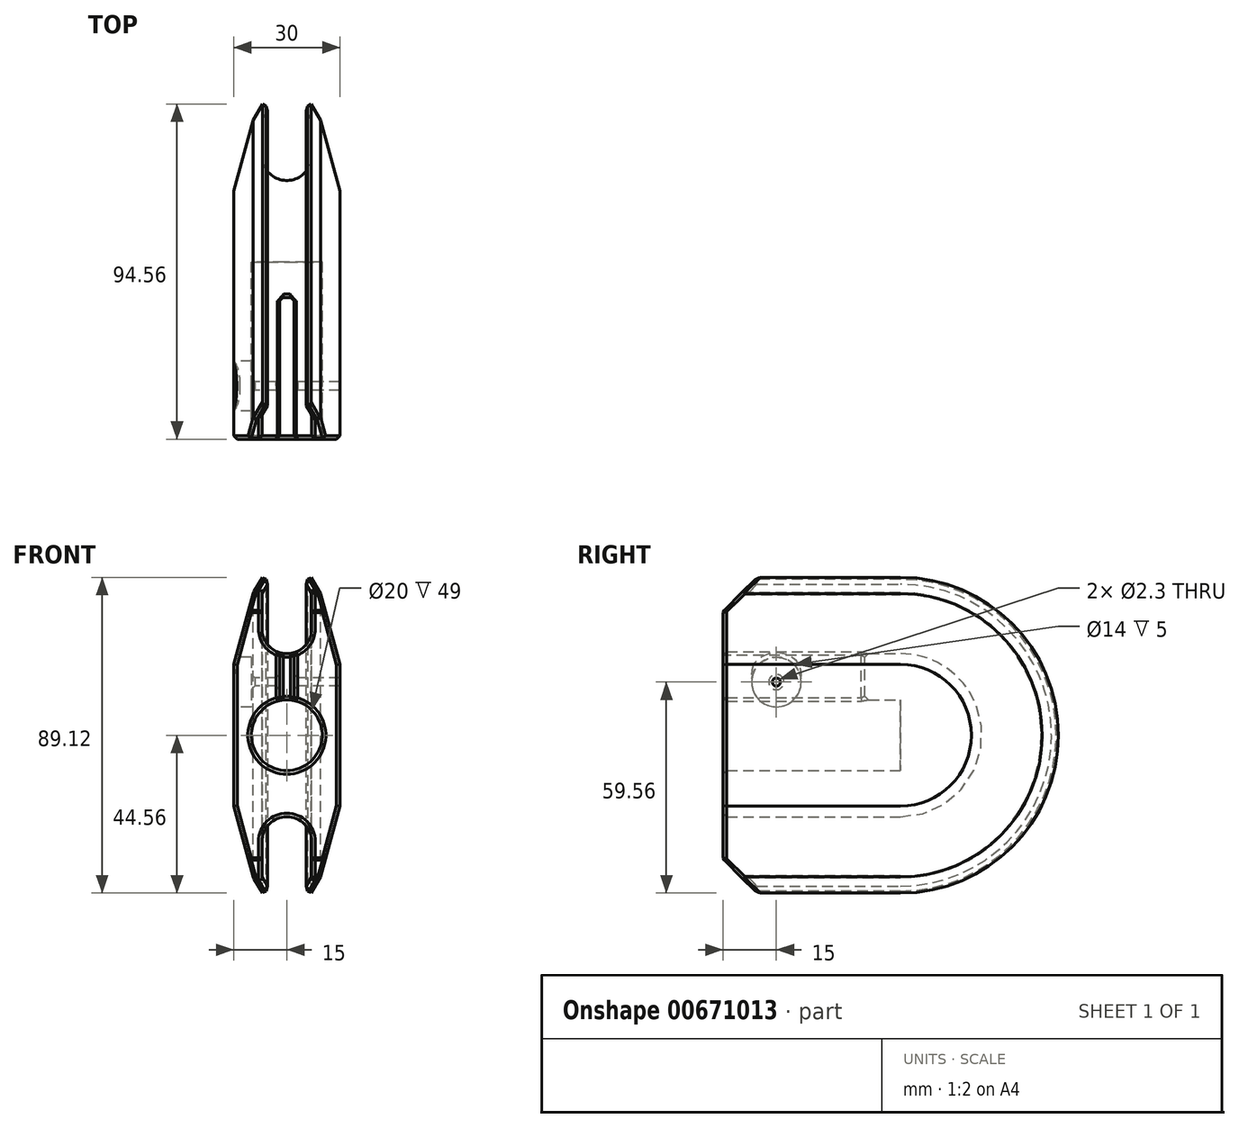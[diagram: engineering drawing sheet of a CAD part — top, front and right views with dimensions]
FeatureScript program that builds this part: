
annotation { "Feature Type Name" : "Feature", "Feature Type Description" : "" }
export const myFeature = defineFeature(function(context is Context, id is Id, definition is map)
    precondition{}
    {
        {
            var Q0;
            Q0=qCreatedBy(makeId("Front.planeOp"),FACE);
            var sketch = newSketch(context, id + "F0", { "sketchPlane" : qUnion([Q0])});
            skCircle(sketch, "E0", {"center": v(0, 0) * mm, "radius": 10 * mm});
            skLineSegment(sketch, "E1", {"start": v(-59.38, 0) * mm, "end": v(62.6, 0) * mm, "construction": true});
            skLineSegment(sketch, "E2", {"start": v(0, 56) * mm, "end": v(0, -52.42) * mm, "construction": true});
            skArc(sketch, "E3", {"start": v(-7, 30) * mm, "mid": v(0, 23) * mm, "end": v(7, 30) * mm});
            skLineSegment(sketch, "E4", {"start": v(7, 30) * mm, "end": v(7, 40) * mm});
            skLineSegment(sketch, "E5", {"start": v(7, 40) * mm, "end": v(5, 43.46) * mm});
            skLineSegment(sketch, "E6", {"start": v(5, 43.46) * mm, "end": v(6.9, 44.56) * mm});
            skLineSegment(sketch, "E7", {"start": v(6.9, 44.56) * mm, "end": v(9.54, 40) * mm});
            skLineSegment(sketch, "E8", {"start": v(9.54, 40) * mm, "end": v(15, 20) * mm});
            skLineSegment(sketch, "E9.MirrorCS", {"start": v(-9.54, 40) * mm, "end": v(-15, 20) * mm});
            skLineSegment(sketch, "E10.MirrorCS", {"start": v(-7, 30) * mm, "end": v(-7, 40) * mm});
            skLineSegment(sketch, "E11.MirrorCS", {"start": v(-5, 43.46) * mm, "end": v(-6.9, 44.56) * mm});
            skLineSegment(sketch, "E12.MirrorCS", {"start": v(-7, 40) * mm, "end": v(-5, 43.46) * mm});
            skLineSegment(sketch, "E13.MirrorCS", {"start": v(-6.9, 44.56) * mm, "end": v(-9.54, 40) * mm});
            skLineSegment(sketch, "E14.MirrorCS", {"start": v(-6.9, -44.56) * mm, "end": v(-9.54, -40) * mm});
            skLineSegment(sketch, "E15.MirrorCS", {"start": v(-7, -40) * mm, "end": v(-5, -43.46) * mm});
            skLineSegment(sketch, "E16.MirrorCS", {"start": v(-5, -43.46) * mm, "end": v(-6.9, -44.56) * mm});
            skLineSegment(sketch, "E17.MirrorCS", {"start": v(6.9, -44.56) * mm, "end": v(9.54, -40) * mm});
            skLineSegment(sketch, "E18.MirrorCS", {"start": v(7, -40) * mm, "end": v(5, -43.46) * mm});
            skLineSegment(sketch, "E19.MirrorCS", {"start": v(5, -43.46) * mm, "end": v(6.9, -44.56) * mm});
            skLineSegment(sketch, "E20.MirrorCS", {"start": v(-7, -30) * mm, "end": v(-7, -40) * mm});
            skLineSegment(sketch, "E21.MirrorCS", {"start": v(-9.54, -40) * mm, "end": v(-15, -20) * mm});
            skLineSegment(sketch, "E22.MirrorCS", {"start": v(9.54, -40) * mm, "end": v(15, -20) * mm});
            skLineSegment(sketch, "E23.MirrorCS", {"start": v(7, -30) * mm, "end": v(7, -40) * mm});
            skArc(sketch, "E24.MirrorCS", {"start": v(-7, -30) * mm, "mid": v(0, -23) * mm, "end": v(7, -30) * mm});
            skLineSegment(sketch, "E25", {"start": v(-15, 0) * mm, "end": v(15, 0) * mm});
            skLineSegment(sketch, "E26", {"start": v(-15, 20) * mm, "end": v(-15, -20) * mm});
            skLineSegment(sketch, "E27", {"start": v(15, 20) * mm, "end": v(15, -20) * mm});
            skSolve(sketch);
        }
        {
            var Q0;
            Q0 = qSketchRegion(id + "F0", true);
            extrude(context, id + "F1", {"entities" : qUnion([Q0]), "depth" : 50 * mm, "offsetDistance" : 25 * mm});
        }
        {
            var Q0;
            Q0=makeQuery(id+"F0.imprint","IMPRINT",FACE,{"disambiguationData":[TD([[makeQuery(id+"F0.imprint","IMPRINT",EDGE,{"derivedFrom":sQuery(id+"F0.wireOp",EDGE,"E3")}),-1.0]])]});
            var Q1;
            {var subQ0=sQuery(id+"F0.wireOp",EDGE,"E25");var subQ1=sQuery(id+"F0.wireOp",EDGE,"E0");var subQ2=makeQuery(id+"F0.imprint","INTERSECT",VERTEX,{"disambiguationData":[OD(0.0)],"derivedFrom":[subQ1,subQ0]});Q1=makeQuery(id+"F0.imprint","IMPRINT",FACE,{"disambiguationData":[TD([[makeQuery(id+"F0.imprint","IMPRINT",EDGE,{"disambiguationData":[TD([[subQ2,1.0]])],"derivedFrom":subQ1}),1.0]])]});}
            var Q2;
            Q2=sQuery(id+"F0.wireOp",EDGE,"E1");
            revolve(context, id + "F2", {"operationType" : NewBodyOperationType.ADD, "entities" : qUnion([Q0, Q1]), "axis" : qUnion([Q2]), "revolveType" : RevolveType.ONE_DIRECTION, "oppositeDirection" : true, "angle" : 180 * degree});
        }
        {
            var Q0;
            {var subQ0=sQuery(id+"F0.wireOp",EDGE,"E26");Q0=makeQuery(id+"F2.boolean.opBoolean","MERGE",FACE,{"derivedFrom":[makeQuery(id+"F1.opExtrude","SWEPT_FACE",FACE,{"disambiguationData":[OSD([subQ0])]}),makeQuery(id+"F2.opRevolve","SWEPT_FACE",FACE,{"disambiguationData":[OSD([subQ0])]})]});}
            var sketch = newSketch(context, id + "F3", { "sketchPlane" : qUnion([Q0])});
            skLineSegment(sketch, "E28", {"start": v(50, 44.56) * mm, "end": v(50, 35) * mm});
            skLineSegment(sketch, "E29", {"start": v(50, 35) * mm, "end": v(40.44, 44.56) * mm});
            skLineSegment(sketch, "E30", {"start": v(40.44, 44.56) * mm, "end": v(50, 44.56) * mm});
            skLineSegment(sketch, "E31.MirrorCS", {"start": v(40.44, -44.56) * mm, "end": v(50, -44.56) * mm});
            skLineSegment(sketch, "E32.MirrorCS", {"start": v(50, -44.56) * mm, "end": v(50, -35) * mm});
            skLineSegment(sketch, "E33.MirrorCS", {"start": v(50, -35) * mm, "end": v(40.44, -44.56) * mm});
            skSolve(sketch);
        }
        {
            var Q0;
            Q0 = qSketchRegion(id + "F3", true);
            extrude(context, id + "F4", {"entities" : qUnion([Q0]), "operationType" : NewBodyOperationType.REMOVE, "endBound" : BoundingType.THROUGH_ALL, "oppositeDirection" : true, "depth" : 25 * mm, "offsetDistance" : 25 * mm});
        }
        {
            var Q0;
            {var subQ0=sQuery(id+"F0.wireOp",EDGE,"E26");Q0=makeQuery(id+"F2.boolean.opBoolean","MERGE",FACE,{"derivedFrom":[makeQuery(id+"F1.opExtrude","SWEPT_FACE",FACE,{"disambiguationData":[OSD([subQ0])]}),makeQuery(id+"F2.opRevolve","SWEPT_FACE",FACE,{"disambiguationData":[OSD([subQ0])]})]});}
            var sketch = newSketch(context, id + "F5", { "sketchPlane" : qUnion([Q0])});
            skCircle(sketch, "E34", {"center": v(35, 15) * mm, "radius": 1.15 * mm});
            skCircle(sketch, "E35", {"center": v(35, 15) * mm, "radius": 7 * mm});
            skSolve(sketch);
        }
        {
            var Q0;
            Q0=makeQuery(id+"F5.imprint","IMPRINT",FACE,{"disambiguationData":[TD([[makeQuery(id+"F5.imprint","IMPRINT",EDGE,{"derivedFrom":sQuery(id+"F5.wireOp",EDGE,"E34")}),1.0]])]});
            extrude(context, id + "F6", {"entities" : qUnion([Q0]), "operationType" : NewBodyOperationType.REMOVE, "endBound" : BoundingType.THROUGH_ALL, "oppositeDirection" : true, "depth" : 25 * mm, "offsetDistance" : 25 * mm});
        }
        {
            var Q0;
            Q0=makeQuery(id+"F5.imprint","IMPRINT",FACE,{"disambiguationData":[TD([[makeQuery(id+"F5.imprint","IMPRINT",EDGE,{"derivedFrom":sQuery(id+"F5.wireOp",EDGE,"E34")}),-1.0]])]});
            var Q1;
            {var subQ0=sQuery(id+"F5.wireOp",EDGE,"E35");var subQ1=makeQuery(id+"F1.opExtrude","SWEPT_EDGE",EDGE,{"disambiguationData":[OSD([sQuery(id+"F0.wireOp",EDGE,"E9.MirrorCS"),sQuery(id+"F0.wireOp",EDGE,"E26")])]});var subQ2=makeQuery(id+"F5.imprint","INTERSECT",VERTEX,{"disambiguationData":[OD(0.0)],"derivedFrom":[subQ1,subQ0]});Q1=makeQuery(id+"F5.imprint","IMPRINT",FACE,{"disambiguationData":[TD([[makeQuery(id+"F5.imprint","IMPRINT",EDGE,{"disambiguationData":[TD([[subQ2,-1.0]])],"derivedFrom":subQ0}),1.0]])]});}
            extrude(context, id + "F7", {"entities" : qUnion([Q0, Q1]), "operationType" : NewBodyOperationType.REMOVE, "oppositeDirection" : true, "depth" : 5 * mm, "offsetDistance" : 25 * mm});
        }
        {
            var Q0;
            Q0=qCreatedBy(makeId("Right.planeOp"),FACE);
            var sketch = newSketch(context, id + "F8", { "sketchPlane" : qUnion([Q0])});
            skLineSegment(sketch, "E36.bottom", {"start": v(-10, 0) * mm, "end": v(-50, 0) * mm});
            skLineSegment(sketch, "E36.top", {"start": v(-10, 44.56) * mm, "end": v(-50, 44.56) * mm});
            skLineSegment(sketch, "E36.left", {"start": v(-10, 0) * mm, "end": v(-10, 44.56) * mm});
            skLineSegment(sketch, "E36.right", {"start": v(-50, 0) * mm, "end": v(-50, 44.56) * mm});
            skSolve(sketch);
        }
        {
            var Q0;
            Q0 = qSketchRegion(id + "F8", true);
            extrude(context, id + "F9", {"entities" : qUnion([Q0]), "operationType" : NewBodyOperationType.REMOVE, "endBound" : BoundingType.SYMMETRIC, "oppositeDirection" : true, "depth" : 4 * mm, "offsetDistance" : 25 * mm});
        }
        {
            var Q0;
            Q0=makeQuery(id+"F1.opExtrude","CAP_FACE",FACE,{"disambiguationData":[OSD([sQuery(id+"F0.wireOp",EDGE,"E0"),sQuery(id+"F0.wireOp",EDGE,"E3"),sQuery(id+"F0.wireOp",EDGE,"E4"),sQuery(id+"F0.wireOp",EDGE,"E5"),sQuery(id+"F0.wireOp",EDGE,"E6"),sQuery(id+"F0.wireOp",EDGE,"E7"),sQuery(id+"F0.wireOp",EDGE,"E8"),sQuery(id+"F0.wireOp",EDGE,"E9.MirrorCS"),sQuery(id+"F0.wireOp",EDGE,"E10.MirrorCS"),sQuery(id+"F0.wireOp",EDGE,"E11.MirrorCS"),sQuery(id+"F0.wireOp",EDGE,"E12.MirrorCS"),sQuery(id+"F0.wireOp",EDGE,"E13.MirrorCS"),sQuery(id+"F0.wireOp",EDGE,"E14.MirrorCS"),sQuery(id+"F0.wireOp",EDGE,"E15.MirrorCS"),sQuery(id+"F0.wireOp",EDGE,"E16.MirrorCS"),sQuery(id+"F0.wireOp",EDGE,"E17.MirrorCS"),sQuery(id+"F0.wireOp",EDGE,"E18.MirrorCS"),sQuery(id+"F0.wireOp",EDGE,"E19.MirrorCS"),sQuery(id+"F0.wireOp",EDGE,"E20.MirrorCS"),sQuery(id+"F0.wireOp",EDGE,"E21.MirrorCS"),sQuery(id+"F0.wireOp",EDGE,"E22.MirrorCS"),sQuery(id+"F0.wireOp",EDGE,"E23.MirrorCS"),sQuery(id+"F0.wireOp",EDGE,"E24.MirrorCS"),sQuery(id+"F0.wireOp",EDGE,"E26"),sQuery(id+"F0.wireOp",EDGE,"E27")])],"isStart":false});
            var Q1;
            Q1=makeQuery(id+"F1.opExtrude","SWEPT_EDGE",EDGE,{"disambiguationData":[OSD([sQuery(id+"F0.wireOp",EDGE,"E15.MirrorCS"),sQuery(id+"F0.wireOp",EDGE,"E16.MirrorCS")])]});
            var Q2;
            Q2=makeQuery(id+"F1.opExtrude","SWEPT_EDGE",EDGE,{"disambiguationData":[OSD([sQuery(id+"F0.wireOp",EDGE,"E18.MirrorCS"),sQuery(id+"F0.wireOp",EDGE,"E23.MirrorCS")])]});
            var Q3;
            Q3=makeQuery(id+"F1.opExtrude","SWEPT_EDGE",EDGE,{"disambiguationData":[OSD([sQuery(id+"F0.wireOp",EDGE,"E5"),sQuery(id+"F0.wireOp",EDGE,"E6")])]});
            var Q4;
            Q4=makeQuery(id+"F1.opExtrude","SWEPT_EDGE",EDGE,{"disambiguationData":[OSD([sQuery(id+"F0.wireOp",EDGE,"E11.MirrorCS"),sQuery(id+"F0.wireOp",EDGE,"E12.MirrorCS")])]});
            var Q5;
            {var subQ2=sQuery(id+"F0.wireOp",EDGE,"E9.MirrorCS");Q5=makeQuery(id+"F4.boolean.opBoolean","COPY",FACE,{"disambiguationData":[TD([makeQuery(id+"F1.opExtrude","SWEPT_FACE",FACE,{"disambiguationData":[OSD([subQ2])]})])],"derivedFrom":makeQuery(id+"F4.opExtrude","SWEPT_FACE",FACE,{"disambiguationData":[OSD([sQuery(id+"F3.wireOp",EDGE,"E29")])]})});}
            var Q6;
            {var subQ1=sQuery(id+"F0.wireOp",EDGE,"E4");Q6=makeQuery(id+"F4.boolean.opBoolean","COPY",FACE,{"disambiguationData":[TD([makeQuery(id+"F1.opExtrude","SWEPT_FACE",FACE,{"disambiguationData":[OSD([subQ1])]})])],"derivedFrom":makeQuery(id+"F4.opExtrude","SWEPT_FACE",FACE,{"disambiguationData":[OSD([sQuery(id+"F3.wireOp",EDGE,"E29")])]})});}
            var Q7;
            {var subQ1=sQuery(id+"F0.wireOp",EDGE,"E4");Q7=makeQuery(id+"F4.boolean.opBoolean","COPY",FACE,{"disambiguationData":[TD([makeQuery(id+"F1.opExtrude","SWEPT_FACE",FACE,{"disambiguationData":[OSD([subQ1])]})])],"derivedFrom":makeQuery(id+"F4.opExtrude","SWEPT_FACE",FACE,{"disambiguationData":[OSD([sQuery(id+"F3.wireOp",EDGE,"E33.MirrorCS")])]})});}
            var Q8;
            {var subQ2=sQuery(id+"F0.wireOp",EDGE,"E10.MirrorCS");Q8=makeQuery(id+"F4.boolean.opBoolean","COPY",FACE,{"disambiguationData":[TD([makeQuery(id+"F1.opExtrude","SWEPT_FACE",FACE,{"disambiguationData":[OSD([subQ2])]})])],"derivedFrom":makeQuery(id+"F4.opExtrude","SWEPT_FACE",FACE,{"disambiguationData":[OSD([sQuery(id+"F3.wireOp",EDGE,"E33.MirrorCS")])]})});}
            var Q9;
            Q9=makeQuery(id+"F7.boolean.opBoolean","COPY",EDGE,{"derivedFrom":makeQuery(id+"F7.opExtrude","CAP_EDGE",EDGE,{"disambiguationData":[OSD([sQuery(id+"F5.wireOp",EDGE,"E35")])],"isStart":true})});
            var Q10;
            Q10=makeQuery(id+"F7.boolean.opBoolean","INTERSECT",EDGE,{"derivedFrom":[makeQuery(id+"F1.opExtrude","SWEPT_FACE",FACE,{"disambiguationData":[OSD([sQuery(id+"F0.wireOp",EDGE,"E9.MirrorCS")])]}),makeQuery(id+"F7.opExtrude","SWEPT_FACE",FACE,{"disambiguationData":[OSD([sQuery(id+"F5.wireOp",EDGE,"E35")])]})]});
            var Q11;
            {var subQ0=sQuery(id+"F5.wireOp",EDGE,"E34");Q11=makeQuery(id+"F9.boolean.opBoolean","SPLIT",FACE,{"disambiguationData":[TD([makeQuery(id+"F7.boolean.opBoolean","COPY",FACE,{"derivedFrom":makeQuery(id+"F7.opExtrude","CAP_FACE",FACE,{"disambiguationData":[OSD([subQ0,sQuery(id+"F5.wireOp",EDGE,"E35")])],"isStart":false})})])],"derivedFrom":makeQuery(id+"F6.boolean.opBoolean","COPY",FACE,{"derivedFrom":makeQuery(id+"F6.opExtrude","SWEPT_FACE",FACE,{"disambiguationData":[OSD([subQ0])]})})});}
            var Q12;
            {var subQ0=sQuery(id+"F5.wireOp",EDGE,"E34");Q12=makeQuery(id+"F9.boolean.opBoolean","SPLIT",FACE,{"disambiguationData":[TD([makeQuery(id+"FHyMzde53jYYuHj_1.1.F7.boolean.opBoolean","COPY",FACE,{"derivedFrom":makeQuery(id+"FHyMzde53jYYuHj_1.1.F7.opExtrude","CAP_FACE",FACE,{"disambiguationData":[OSD([subQ0,sQuery(id+"F5.wireOp",EDGE,"E35")])],"isStart":false})})])],"derivedFrom":makeQuery(id+"F6.boolean.opBoolean","COPY",FACE,{"derivedFrom":makeQuery(id+"F6.opExtrude","SWEPT_FACE",FACE,{"disambiguationData":[OSD([subQ0])]})})});}
            var Q13;
            Q13=makeQuery(id+"FHyMzde53jYYuHj_1.1.F7.boolean.opBoolean","INTERSECT",EDGE,{"derivedFrom":[makeQuery(id+"F1.opExtrude","SWEPT_FACE",FACE,{"disambiguationData":[OSD([sQuery(id+"F0.wireOp",EDGE,"E8")])]}),makeQuery(id+"FHyMzde53jYYuHj_1.1.F7.opExtrude","SWEPT_FACE",FACE,{"disambiguationData":[OSD([sQuery(id+"F5.wireOp",EDGE,"E35")])]})]});
            var Q14;
            Q14=makeQuery(id+"FHyMzde53jYYuHj_1.1.F7.boolean.opBoolean","COPY",EDGE,{"derivedFrom":makeQuery(id+"FHyMzde53jYYuHj_1.1.F7.opExtrude","CAP_EDGE",EDGE,{"disambiguationData":[OSD([sQuery(id+"F5.wireOp",EDGE,"E35")])],"isStart":true})});
            var Q15;
            Q15=makeQuery(id+"F9.boolean.opBoolean","COPY",FACE,{"derivedFrom":makeQuery(id+"F9.opExtrude","CAP_FACE",FACE,{"disambiguationData":[OSD([sQuery(id+"F8.wireOp",EDGE,"E36.bottom"),sQuery(id+"F8.wireOp",EDGE,"E36.top"),sQuery(id+"F8.wireOp",EDGE,"E36.left"),sQuery(id+"F8.wireOp",EDGE,"E36.right")])],"isStart":true})});
            var Q16;
            Q16=makeQuery(id+"F9.boolean.opBoolean","COPY",FACE,{"derivedFrom":makeQuery(id+"F9.opExtrude","CAP_FACE",FACE,{"disambiguationData":[OSD([sQuery(id+"F8.wireOp",EDGE,"E36.bottom"),sQuery(id+"F8.wireOp",EDGE,"E36.top"),sQuery(id+"F8.wireOp",EDGE,"E36.left"),sQuery(id+"F8.wireOp",EDGE,"E36.right")])],"isStart":false})});
            chamfer(context, id + "F10", {"entities" : qUnion([Q0, Q1, Q2, Q3, Q4, Q5, Q6, Q7, Q8, Q9, Q10, Q11, Q12, Q13, Q14, Q15, Q16]), "width" : 1 * mm, "tangentPropagation" : true});
        }
    });
